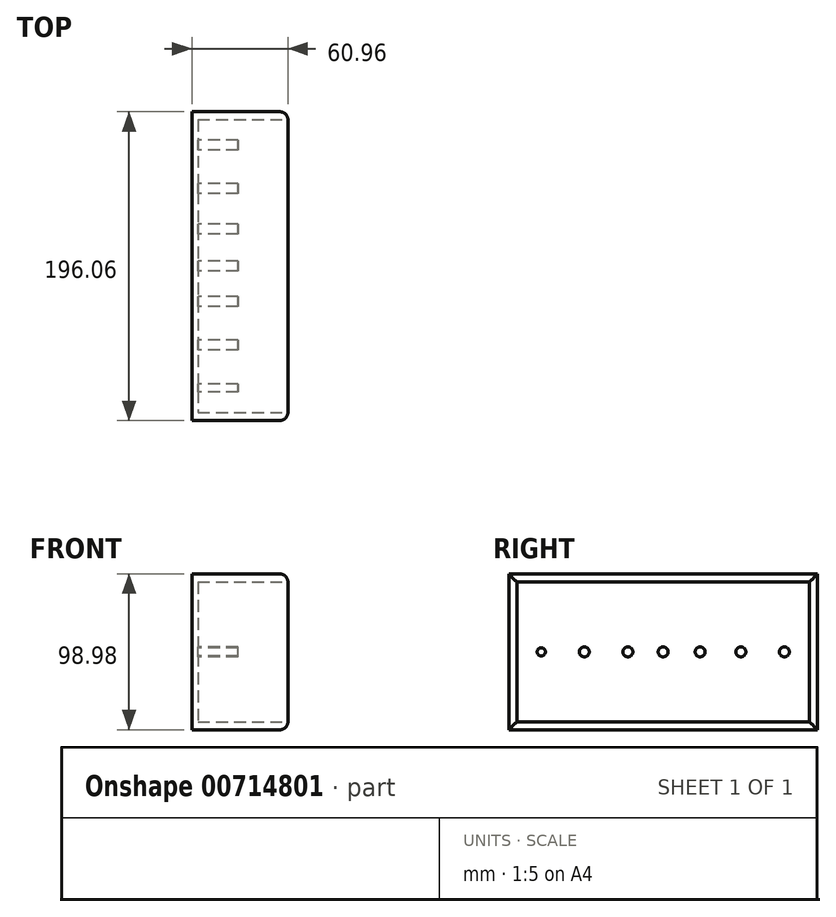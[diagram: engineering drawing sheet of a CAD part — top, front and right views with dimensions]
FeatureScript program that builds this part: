
annotation { "Feature Type Name" : "Feature", "Feature Type Description" : "" }
export const myFeature = defineFeature(function(context is Context, id is Id, definition is map)
    precondition{}
    {
        {
            var Q0;
            Q0=qCreatedBy(makeId("Right.planeOp"),FACE);
            var sketch = newSketch(context, id + "F0", { "sketchPlane" : qUnion([Q0])});
            skLineSegment(sketch, "E0.bottom", {"start": v(98.03, 49.5) * mm, "end": v(-98.03, 49.5) * mm});
            skLineSegment(sketch, "E0.top", {"start": v(98.03, -49.5) * mm, "end": v(-98.03, -49.5) * mm});
            skLineSegment(sketch, "E0.left", {"start": v(98.03, 49.5) * mm, "end": v(98.03, -49.5) * mm});
            skLineSegment(sketch, "E0.right", {"start": v(-98.03, 49.5) * mm, "end": v(-98.03, -49.5) * mm});
            skPoint(sketch, "E0.middle", {"position": v(0, 0) * mm});
            skSolve(sketch);
        }
        {
            var Q0;
            Q0=makeQuery(id+"F0.imprint","IMPRINT",FACE,{"disambiguationData":[TD([[makeQuery(id+"F0.imprint","IMPRINT",EDGE,{"derivedFrom":sQuery(id+"F0.wireOp",EDGE,"E0.bottom")}),1.0]])]});
            extrude(context, id + "F1", {"entities" : qUnion([Q0]), "depth" : 60.96 * mm, "offsetDistance" : 25.4 * mm});
        }
        {
            var Q0;
            Q0=makeQuery(id+"F1.opExtrude","CAP_EDGE",EDGE,{"disambiguationData":[OSD([sQuery(id+"F0.wireOp",EDGE,"E0.left")])],"isStart":false});
            var Q1;
            Q1=makeQuery(id+"F1.opExtrude","CAP_EDGE",EDGE,{"disambiguationData":[OSD([sQuery(id+"F0.wireOp",EDGE,"E0.bottom")])],"isStart":false});
            var Q2;
            Q2=makeQuery(id+"F1.opExtrude","CAP_EDGE",EDGE,{"disambiguationData":[OSD([sQuery(id+"F0.wireOp",EDGE,"E0.right")])],"isStart":false});
            var Q3;
            Q3=makeQuery(id+"F1.opExtrude","CAP_EDGE",EDGE,{"disambiguationData":[OSD([sQuery(id+"F0.wireOp",EDGE,"E0.top")])],"isStart":false});
            fillet(context, id + "F2", {"entities" : qUnion([Q0, Q1, Q2, Q3]), "radius" : 5.08 * mm, "tangentPropagation" : true, "allowEdgeOverflow" : false});
        }
        {
            var Q0;
            Q0=makeQuery(id+"F1.opExtrude","CAP_FACE",FACE,{"disambiguationData":[OSD([sQuery(id+"F0.wireOp",EDGE,"E0.bottom"),sQuery(id+"F0.wireOp",EDGE,"E0.top"),sQuery(id+"F0.wireOp",EDGE,"E0.left"),sQuery(id+"F0.wireOp",EDGE,"E0.right")])],"isStart":false});
            var sketch = newSketch(context, id + "F3", { "sketchPlane" : qUnion([Q0])});
            skLineSegment(sketch, "E1.bottom", {"start": v(92.95, 44.41) * mm, "end": v(-92.95, 44.41) * mm});
            skLineSegment(sketch, "E1.top", {"start": v(92.95, -44.41) * mm, "end": v(-92.95, -44.41) * mm});
            skLineSegment(sketch, "E1.left", {"start": v(92.95, 44.41) * mm, "end": v(92.95, -44.41) * mm});
            skLineSegment(sketch, "E1.right", {"start": v(-92.95, 44.41) * mm, "end": v(-92.95, -44.41) * mm});
            skPoint(sketch, "E1.middle", {"position": v(0, 0) * mm});
            skSolve(sketch);
        }
        {
            var Q0;
            Q0=makeQuery(id+"F3.imprint","IMPRINT",FACE,{"disambiguationData":[TD([[makeQuery(id+"F3.imprint","IMPRINT",EDGE,{"derivedFrom":sQuery(id+"F3.wireOp",EDGE,"E1.bottom")}),1.0]])]});
            extrude(context, id + "F4", {"entities" : qUnion([Q0]), "operationType" : NewBodyOperationType.REMOVE, "oppositeDirection" : true, "depth" : 57.15 * mm, "offsetDistance" : 25.4 * mm});
        }
        {
            var Q0;
            Q0=makeQuery(id+"F4.boolean.opBoolean","COPY",FACE,{"derivedFrom":makeQuery(id+"F4.opExtrude","CAP_FACE",FACE,{"disambiguationData":[OSD([sQuery(id+"F3.wireOp",EDGE,"E1.bottom"),sQuery(id+"F3.wireOp",EDGE,"E1.top"),sQuery(id+"F3.wireOp",EDGE,"E1.left"),sQuery(id+"F3.wireOp",EDGE,"E1.right")])],"isStart":false})});
            var sketch = newSketch(context, id + "F5", { "sketchPlane" : qUnion([Q0])});
            skPoint(sketch, "E2", {"position": v(0, 0) * mm});
            skPoint(sketch, "E3", {"position": v(23.02, 0) * mm});
            skPoint(sketch, "E4", {"position": v(48.02, 0) * mm});
            skPoint(sketch, "E5", {"position": v(75.08, 0) * mm});
            skPoint(sketch, "E6", {"position": v(-21.1, 0) * mm});
            skPoint(sketch, "E7", {"position": v(-47.58, 0) * mm});
            skPoint(sketch, "E8", {"position": v(-75.82, 0) * mm});
            skSolve(sketch);
        }
        {
            var Q0;
            Q0=makeQuery(id+"F5.imprint","IMPRINT",FACE,{"disambiguationData":[TD([[makeQuery(id+"F5.imprint","IMPRINT",EDGE,{"derivedFrom":makeQuery(id+"F4.boolean.opBoolean","COPY",EDGE,{"derivedFrom":makeQuery(id+"F4.opExtrude","CAP_EDGE",EDGE,{"disambiguationData":[OSD([sQuery(id+"F3.wireOp",EDGE,"E1.bottom")])],"isStart":false})})}),1.0]])]});
            var sketch = newSketch(context, id + "F6", { "sketchPlane" : qUnion([Q0])});
            skCircle(sketch, "E9", {"center": v(0, 0) * mm, "radius": 3.18 * mm});
            skCircle(sketch, "E10", {"center": v(23.49, 0) * mm, "radius": 3.18 * mm});
            skCircle(sketch, "E11", {"center": v(49.33, 0) * mm, "radius": 3.18 * mm});
            skCircle(sketch, "E12", {"center": v(77, 0) * mm, "radius": 3.18 * mm});
            skCircle(sketch, "E13", {"center": v(-22.42, 0) * mm, "radius": 3.18 * mm});
            skCircle(sketch, "E14", {"center": v(-50.09, 0) * mm, "radius": 3.18 * mm});
            skCircle(sketch, "E15", {"center": v(-77.4, 0) * mm, "radius": 2.6 * mm});
            skSolve(sketch);
        }
        {
            var Q0;
            Q0 = qSketchRegion(id + "F6", true);
            extrude(context, id + "F7", {"entities" : qUnion([Q0]), "operationType" : NewBodyOperationType.ADD, "depth" : 25.4 * mm, "offsetDistance" : 25.4 * mm});
        }
    });
